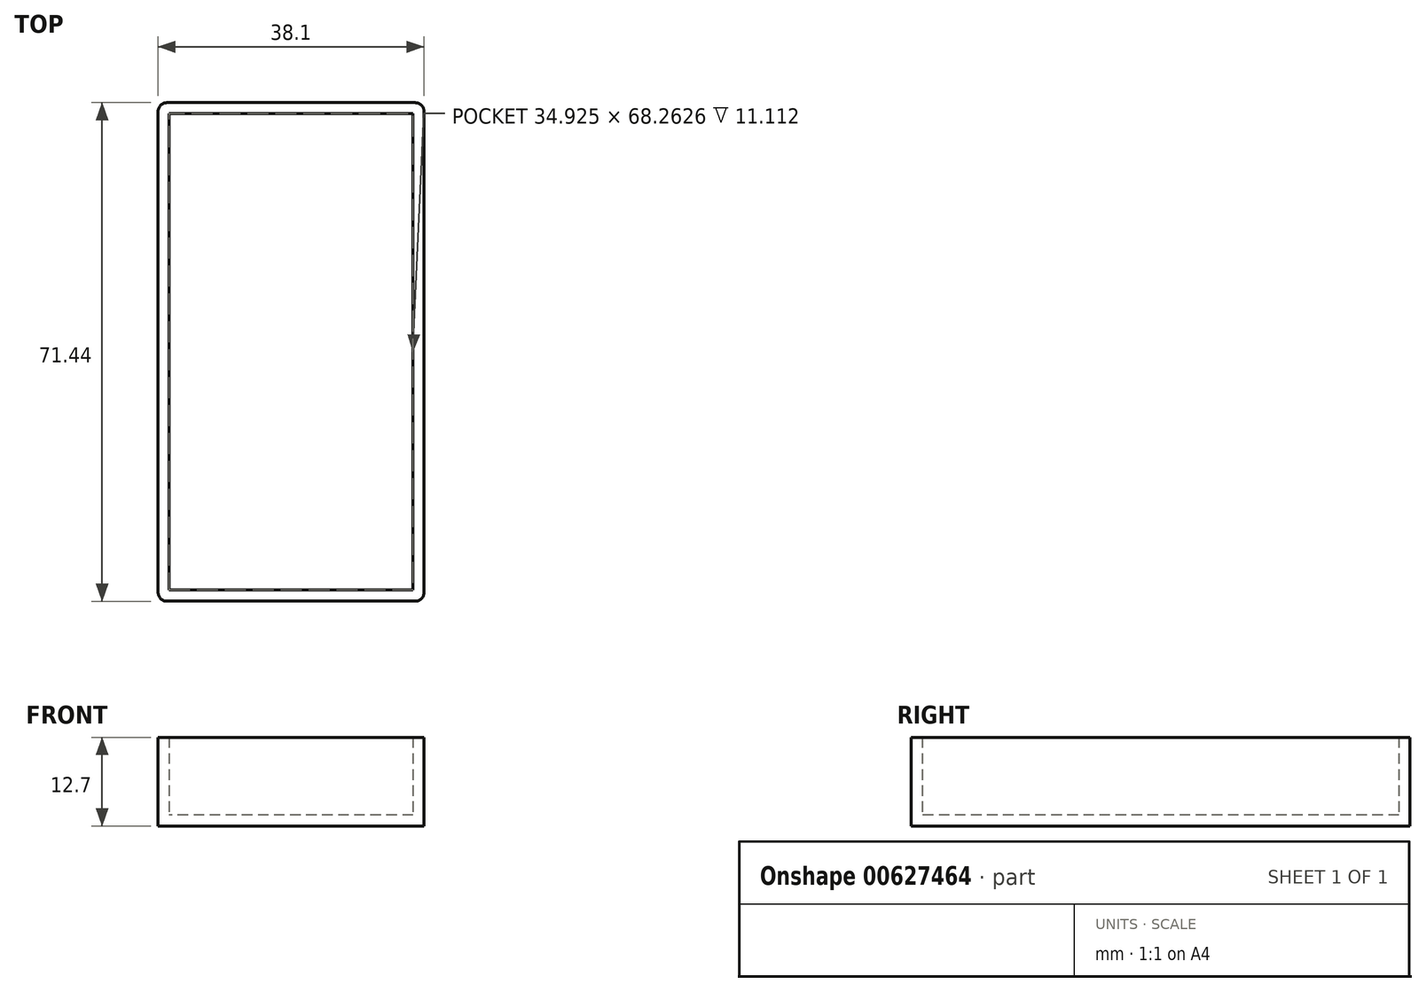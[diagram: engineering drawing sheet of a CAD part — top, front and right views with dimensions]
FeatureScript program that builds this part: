
annotation { "Feature Type Name" : "Feature", "Feature Type Description" : "" }
export const myFeature = defineFeature(function(context is Context, id is Id, definition is map)
    precondition{}
    {
        {
            var Q0;
            Q0=qCreatedBy(makeId("Top.planeOp"),FACE);
            var sketch = newSketch(context, id + "F0", { "sketchPlane" : qUnion([Q0])});
            skLineSegment(sketch, "E0.bottom", {"start": v(19.05, 35.72) * mm, "end": v(-19.05, 35.72) * mm});
            skLineSegment(sketch, "E0.top", {"start": v(19.05, -35.72) * mm, "end": v(-19.05, -35.72) * mm});
            skLineSegment(sketch, "E0.left", {"start": v(19.05, 35.72) * mm, "end": v(19.05, -35.72) * mm});
            skLineSegment(sketch, "E0.right", {"start": v(-19.05, 35.72) * mm, "end": v(-19.05, -35.72) * mm});
            skPoint(sketch, "E0.middle", {"position": v(0, 0) * mm});
            skSolve(sketch);
        }
        {
            var Q0;
            Q0 = qSketchRegion(id + "F0", true);
            extrude(context, id + "F1", {"entities" : qUnion([Q0]), "depth" : 12.7 * mm, "offsetDistance" : 25.4 * mm});
        }
        {
            var Q0;
            Q0=makeQuery(id+"F1.opExtrude","CAP_FACE",FACE,{"disambiguationData":[OSD([sQuery(id+"F0.wireOp",EDGE,"E0.bottom"),sQuery(id+"F0.wireOp",EDGE,"E0.top"),sQuery(id+"F0.wireOp",EDGE,"E0.left"),sQuery(id+"F0.wireOp",EDGE,"E0.right")])],"isStart":false});
            shell(context, id + "F2", {"entities" : qUnion([Q0]), "thickness" : 1.59 * mm});
        }
        {
            var Q0;
            Q0=makeQuery(id+"F1.opExtrude","SWEPT_EDGE",EDGE,{"disambiguationData":[OSD([sQuery(id+"F0.wireOp",EDGE,"E0.top"),sQuery(id+"F0.wireOp",EDGE,"E0.right")])]});
            var Q1;
            Q1=makeQuery(id+"F1.opExtrude","SWEPT_EDGE",EDGE,{"disambiguationData":[OSD([sQuery(id+"F0.wireOp",EDGE,"E0.top"),sQuery(id+"F0.wireOp",EDGE,"E0.left")])]});
            var Q2;
            Q2=makeQuery(id+"F1.opExtrude","SWEPT_EDGE",EDGE,{"disambiguationData":[OSD([sQuery(id+"F0.wireOp",EDGE,"E0.bottom"),sQuery(id+"F0.wireOp",EDGE,"E0.right")])]});
            var Q3;
            Q3=makeQuery(id+"F1.opExtrude","SWEPT_EDGE",EDGE,{"disambiguationData":[OSD([sQuery(id+"F0.wireOp",EDGE,"E0.bottom"),sQuery(id+"F0.wireOp",EDGE,"E0.left")])]});
            fillet(context, id + "F3", {"entities" : qUnion([Q0, Q1, Q2, Q3]), "radius" : 1.27 * mm, "tangentPropagation" : true, "allowEdgeOverflow" : false});
        }
    });
